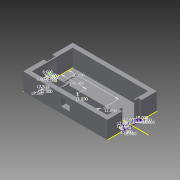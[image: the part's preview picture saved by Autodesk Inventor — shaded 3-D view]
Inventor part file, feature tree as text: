
AUTODESK INVENTOR PART (.ipt)
format: ipt  version: 2014 (Build 180170000, 170)  size: 419,840 bytes
history: native  units: in
note: dims shown in document units (in); Inventor stores cm internally (conversion verified against a paired STEP export)
features: extrude x20, sketch x12, projected_geometry x2
ambient origin geometry x8: Origin, YZ Plane, XZ Plane, XY Plane, X Axis, Y Axis, Z Axis, Center Point
bodies: Body1 (feature_tree)
feature tree (34):
  extrude  "Extrusion9"  Depth=132.0in
  extrude  "Extrusion10"  Depth=57.0in
  extrude  "Extrusion11"  Depth=24.0in
  extrude  "Extrusion12"  Depth=72.0in
  extrude  "Extrusion13"  Depth=24.0in
  extrude  "Extrusion15"  Depth=4.5in
  sketch  "Sketch15"  dims[d34=48.0in d35=114.0in]
  extrude  "Extrusion18"  Depth=168.0in
  extrude  "Extrusion19"  Depth=114.0in
  extrude  "Extrusion20"  Depth=35.0in
  extrude  "Extrusion22"  Depth=468.0in
  extrude  "Extrusion23"  Depth=1.0in TaperAngle=0.0deg
  extrude  "Extrusion24"  Depth=7.5in
  extrude  "Extrusion25"  Depth=7.25in
  extrude  "Extrusion28"  Depth=28.5in
  extrude  "Extrusion29"  Depth=7.5in
  extrude  "Extrusion30"  Depth=7.25in
  sketch  "Sketch20"  dims[d111=16.0in d112=0.0in d113=7.5in d115=7.25in d116=28.5in d117=7.5in d118=7.25in d119=7.5in d120=7.25in d121=7.5in d122=7.25in d123=7.5in d124=7.25in d125=7.5in d126=7.25in d127=7.5in d128=7.25in d129=7.5in d130=7.25in d131=7.5in d132=7.25in d133=7.5in d134=7.25in d135=7.5in d136=7.25in d137=7.5in d138=7.25in d139=7.5in d140=7.25in d141=7.5in d142=7.25in d143=16.0in d144=0.0in d145=48.0in d147=48.0in d148=32.0in d150=16.0in d151=0.0in d152=12.75in d153=0.0in d154=7.25in d155=7.5in d156=1.0in d158=1.0in d159=0.0in d161=12.0in d165=280.0in d166=12.0in d167=17.5in d172=12.0in d173=12.0in d174=6.0in d176=12.0in d177=12.0in d180=12.0in d181=12.0in d184=18.0in d190=1.0in d191=0.0in d192=6.0in d193=6.0in d194=6.0in d195=18.0in d196=18.0in d197=18.0in d198=18.0in d199=36.0in d200=6.0in d201=1.0in d202=0.0in d203=1.0in d204=0.0in d207=80.0in d208=0.0in d209=80.0in d210=0.0in d211=80.0in d212=0.0in d213=1.0in d214=0.0in d215=6.0in d216=36.0in d221=1.0in d222=0.0in d223=1.0in d224=0.0in d225=1.0in d226=0.0in d227=78.375in d228=26.125in d229=24.0in d230=24.0in d231=12.0in d232=17.5in d233=1.0in d234=0.0in d235=5.5in d236=0.0in d237=12.0in d238=140.0in d239=1.0in d240=0.0in]
  extrude  "Extrusion31"  Depth=7.5in
  extrude  "Burners"  Depth=7.25in
  extrude  "Extrusion33"  Depth=7.5in
  extrude  "Extrusion14"  Depth=48.0in
  sketch  "Sketch1"  dims[d0=288.0in d1=480.0in d2=432.0in d3=240.0in d5=132.0in d7=150.0in]
  sketch  "Sketch8"  dims[d11=57.0in d17=216.0in]
  projected_geometry  "Projected Loop5"
  sketch  "Sketch9"  dims[d18=276.0in d19=24.0in]
  projected_geometry  "Projected Loop6"
  sketch  "Sketch10"  dims[d20=24.0in d23=72.0in]
  sketch  "Sketch11"  dims[d24=102.0in d25=24.0in]
  sketch  "Sketch12"  dims[d27=432.0in d28=4.5in]
  sketch  "Sketch14"  dims[d29=0.0in d30=168.0in]
  sketch  "Sketch16"  dims[d36=24.0in d46=35.0in]
  sketch  "Sketch17"  dims[d105=35.0in d106=468.0in]
  sketch  "Sketch18"  dims[d107=96.0in d108=0.0in d109=1.0in d110=0.0in]
